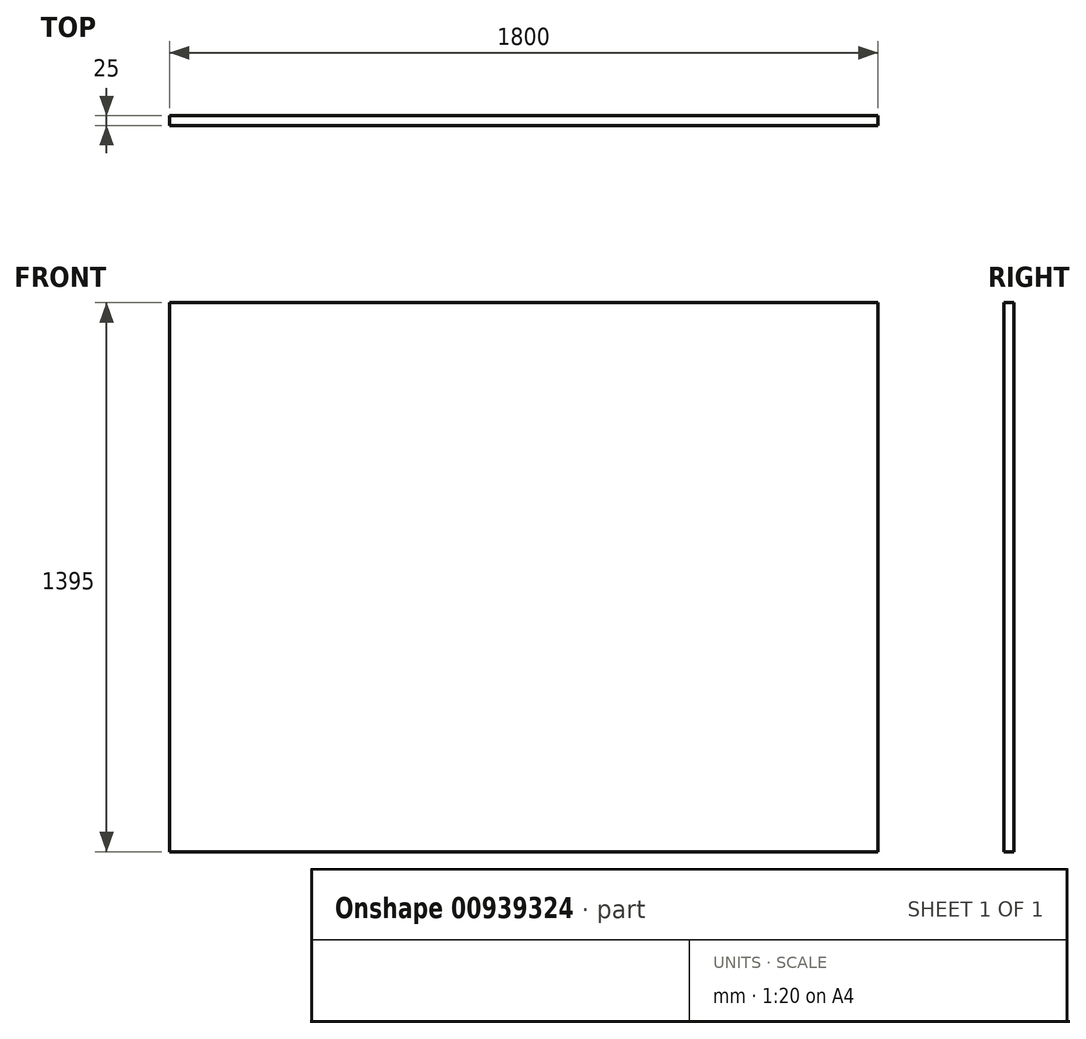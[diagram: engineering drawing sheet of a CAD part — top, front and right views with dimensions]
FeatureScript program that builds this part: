
annotation { "Feature Type Name" : "Feature", "Feature Type Description" : "" }
export const myFeature = defineFeature(function(context is Context, id is Id, definition is map)
    precondition{}
    {
        {
            var Q0;
            Q0=qCreatedBy(makeId("Front.planeOp"),FACE);
            var sketch = newSketch(context, id + "F0", { "sketchPlane" : qUnion([Q0])});
            skLineSegment(sketch, "E0.bottom", {"start": v(0, 0) * mm, "end": v(1800, 0) * mm});
            skLineSegment(sketch, "E0.top", {"start": v(0, 1395) * mm, "end": v(1800, 1395) * mm});
            skLineSegment(sketch, "E0.left", {"start": v(0, 0) * mm, "end": v(0, 1395) * mm});
            skLineSegment(sketch, "E0.right", {"start": v(1800, 0) * mm, "end": v(1800, 1395) * mm});
            skSolve(sketch);
        }
        {
            var Q0;
            Q0 = qSketchRegion(id + "F0", true);
            extrude(context, id + "F1", {"entities" : qUnion([Q0]), "depth" : 25 * mm, "offsetDistance" : 25 * mm});
        }
    });
